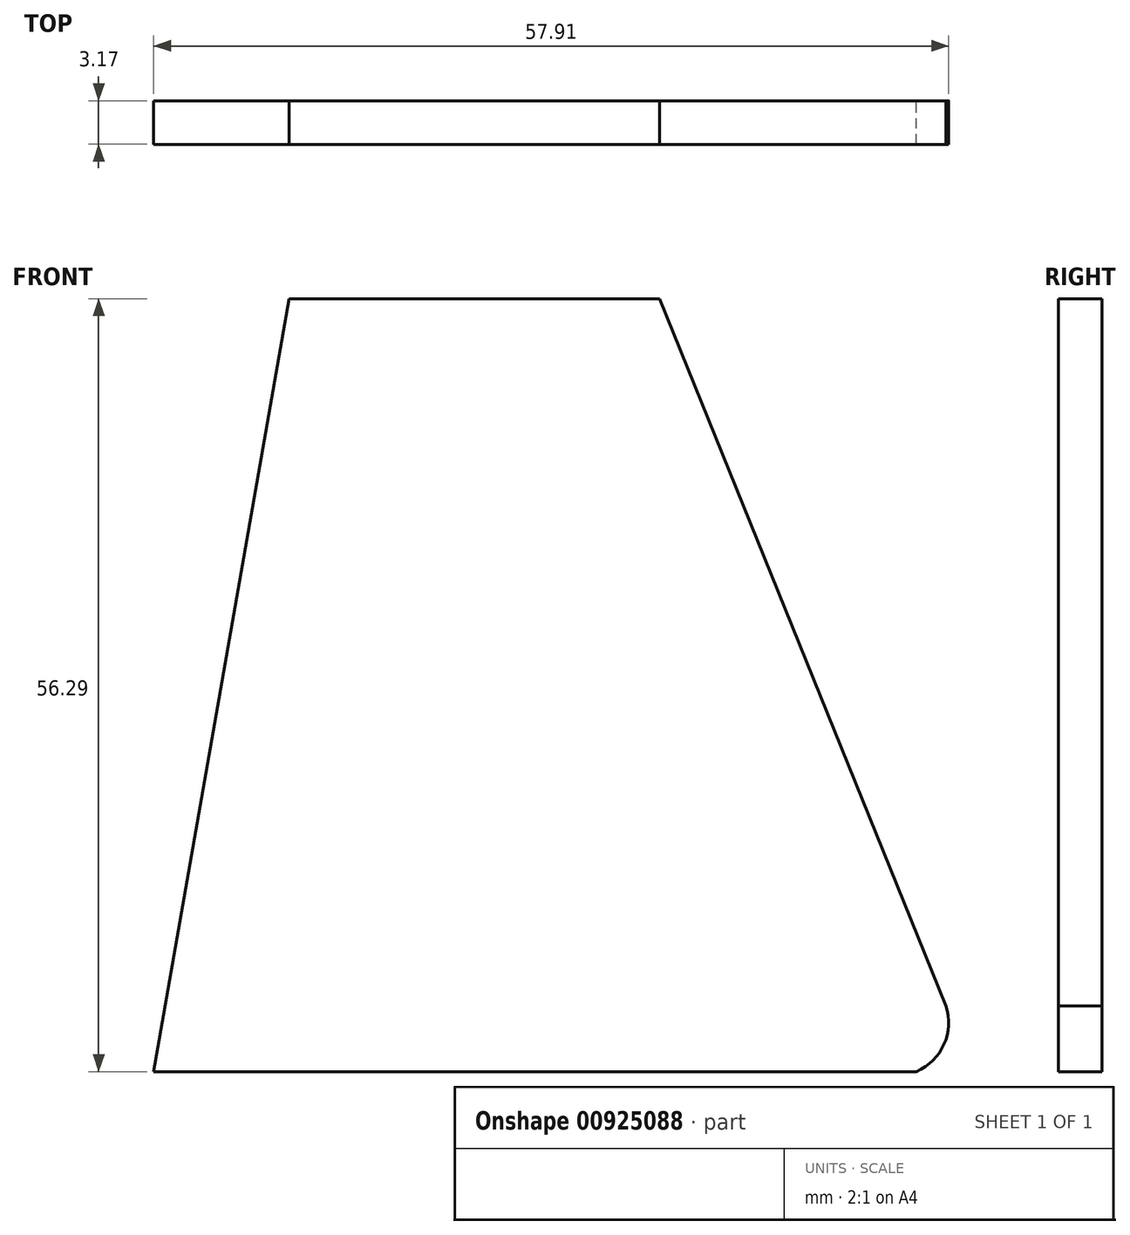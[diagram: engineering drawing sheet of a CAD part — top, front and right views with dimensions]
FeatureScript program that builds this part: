
annotation { "Feature Type Name" : "Feature", "Feature Type Description" : "" }
export const myFeature = defineFeature(function(context is Context, id is Id, definition is map)
    precondition{}
    {
        {
            var Q0;
            Q0=qCreatedBy(makeId("Front.planeOp"),FACE);
            var sketch = newSketch(context, id + "F0", { "sketchPlane" : qUnion([Q0])});
            skLineSegment(sketch, "E0", {"start": v(-27.24, 50.97) * mm, "end": v(-0.26, 50.97) * mm});
            skLineSegment(sketch, "E1", {"start": v(-0.26, 50.97) * mm, "end": v(20.61, -0.53) * mm});
            skLineSegment(sketch, "E2", {"start": v(18.46, -5.32) * mm, "end": v(-37.1, -5.32) * mm});
            skLineSegment(sketch, "E3", {"start": v(-27.24, 50.97) * mm, "end": v(-37.1, -5.32) * mm});
            skArc(sketch, "E4", {"start": v(18.46, -5.32) * mm, "mid": v(20.46, -3.34) * mm, "end": v(20.61, -0.53) * mm});
            skPoint(sketch, "E5.orphan", {"position": v(20.4, 0) * mm});
            skSolve(sketch);
        }
        {
            var Q0;
            Q0 = qSketchRegion(id + "F0", true);
            extrude(context, id + "F1", {"entities" : qUnion([Q0]), "depth" : 3.17 * mm, "offsetDistance" : 25.4 * mm});
        }
    });
